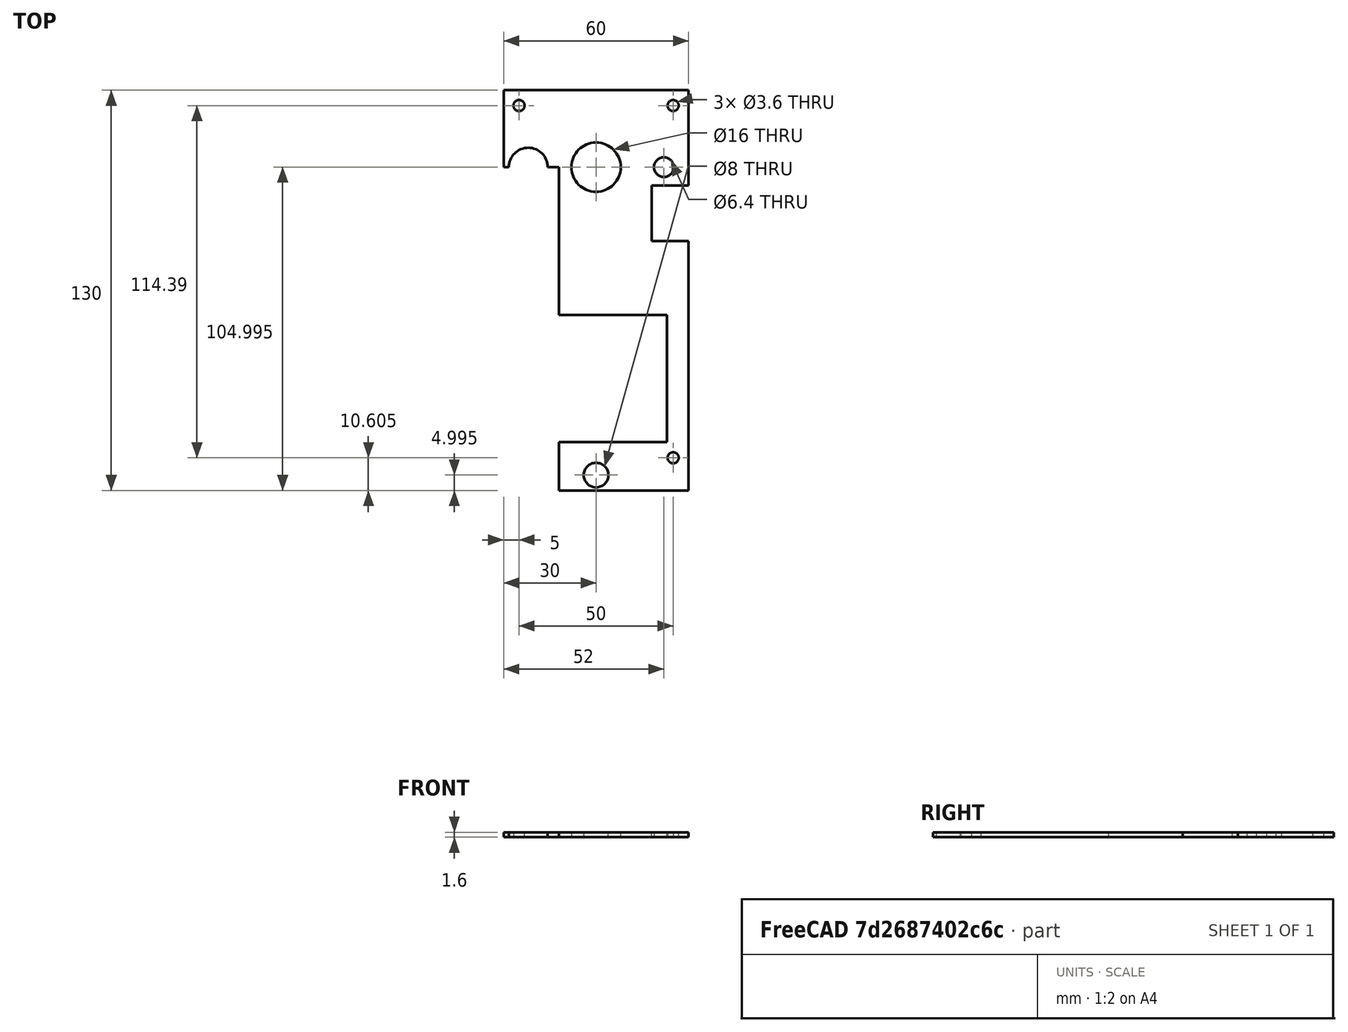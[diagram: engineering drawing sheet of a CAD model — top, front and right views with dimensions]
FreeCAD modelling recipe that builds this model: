
FCSTD DOCUMENT  (FreeCAD 0.18.4R)
Label: acrylic_head_pnp
License: All rights reserved
LicenseURL: http://en.wikipedia.org/wiki/All_rights_reserved
objects: Sketcher::SketchObject×1, PartDesign::Pad×1, PartDesign::Body×1
note: 4 computed .brp shape members not serialized (recipe doc carries the construction recipe); baked Part::Feature solids carry a one-line shape summary decoded from their .brp

FEATURE [Sketcher::SketchObject] Sketch
  MapMode = 5
  Support = -> [XY_Plane]
  sketch-geometry (24):
    g0: Circle CenterX=0 CenterY=39.8952 CenterZ=0 NormalX=0 NormalY=0 NormalZ=1 AngleXU=0 Radius=8
    g1: Circle CenterX=22 CenterY=39.8952 CenterZ=0 NormalX=0 NormalY=0 NormalZ=1 AngleXU=0 Radius=3.2
    g2: ArcOfCircle CenterX=-22 CenterY=39.8952 CenterZ=0 NormalX=0 NormalY=0 NormalZ=1 AngleXU=0 Radius=6.28949 StartAngle=4e-16 EndAngle=3.14159
    g3: LineSegment StartX=-28.2895 StartY=39.8952 StartZ=0 EndX=-30 EndY=39.8952 EndZ=0
    g4: LineSegment StartX=-15.7105 StartY=39.8952 StartZ=0 EndX=-12 EndY=39.8952 EndZ=0
    g5: LineSegment StartX=-30 StartY=39.8952 StartZ=0 EndX=-30 EndY=64.8952 EndZ=0
    g6: LineSegment StartX=-12 StartY=39.8952 StartZ=0 EndX=-12 EndY=-8.10484 EndZ=0
    g7: LineSegment StartX=-12 StartY=-8.10484 StartZ=0 EndX=-3.49057 EndY=-8.10484 EndZ=0
    g8: LineSegment StartX=3.49058 StartY=-8.10484 StartZ=0 EndX=23 EndY=-8.10484 EndZ=0
    g9: LineSegment StartX=23 StartY=-8.10484 StartZ=0 EndX=23 EndY=-49.4148 EndZ=0
    g10: LineSegment StartX=23 StartY=-49.4148 StartZ=0 EndX=-12 EndY=-49.4148 EndZ=0
    g11: LineSegment StartX=-12 StartY=-49.4148 StartZ=0 EndX=-12 EndY=-65.1048 EndZ=0
    g12: LineSegment StartX=30 StartY=-65.1048 StartZ=0 EndX=-12 EndY=-65.1048 EndZ=0
    g13: LineSegment StartX=30 StartY=33.8952 StartZ=0 EndX=18 EndY=33.8952 EndZ=0
    g14: LineSegment StartX=30 StartY=33.8952 StartZ=0 EndX=30 EndY=64.8952 EndZ=0
    g15: LineSegment StartX=18 StartY=33.8952 StartZ=0 EndX=18 EndY=15.8952 EndZ=0
    g16: LineSegment StartX=18 StartY=15.8952 StartZ=0 EndX=30 EndY=15.8952 EndZ=0
    g17: LineSegment StartX=-3.49058 StartY=-8.10484 StartZ=0 EndX=3.49058 EndY=-8.10484 EndZ=0
    g18: Circle CenterX=0 CenterY=-60.1048 CenterZ=0 NormalX=0 NormalY=0 NormalZ=1 AngleXU=0 Radius=4
    g19: Circle CenterX=25 CenterY=-54.4948 CenterZ=0 NormalX=0 NormalY=0 NormalZ=1 AngleXU=0 Radius=1.8
    g20: Circle CenterX=25 CenterY=59.8952 CenterZ=0 NormalX=0 NormalY=0 NormalZ=1 AngleXU=0 Radius=1.8
    g21: LineSegment StartX=30 StartY=15.8952 StartZ=0 EndX=30 EndY=-65.1048 EndZ=0
    g22: LineSegment StartX=-30 StartY=64.8952 StartZ=0 EndX=30 EndY=64.8952 EndZ=0
    g23: Circle CenterX=-25 CenterY=59.8952 CenterZ=0 NormalX=0 NormalY=0 NormalZ=1 AngleXU=0 Radius=1.8
  constraints (63):
    c: PointOnObject(g0,g-2)
    c: Radius(g0) = 8
    c: Radius(g1) = 3.2
    c: Horizontal(g0,g1)
    c: Coincident(g3,g2)
    c: Distance(g1,g2) = 44
    c: Coincident(g4,g2)
    c: Horizontal(g4)
    c: Horizontal(g3,g2)
    c: DistanceX(g3,g4) = 18
    c: Coincident(g5,g3)
    c: Vertical(g5)
    c: Coincident(g6,g4)
    c: Vertical(g6)
    c: DistanceY(g6,g6) = 48
    c: Horizontal(g3,g2)
    c: Horizontal(g0,g4)
    c: Coincident(g7,g6)
    c: Horizontal(g7)
    c: Horizontal(g8)
    c: Coincident(g9,g8)
    c: Vertical(g9)
    c: Coincident(g10,g9)
    c: Horizontal(g10)
    c: DistanceX(g10,g10) = 35
    c: Coincident(g11,g10)
    c: Coincident(g12,g11)
    c: Horizontal(g12)
    c: Horizontal(g13)
    c: Vertical(g14)
    c: Distance(g14) = 31
    c: Distance(g5,g14) = 60
    c: Coincident(g15,g13)
    c: Vertical(g15)
    c: Coincident(g16,g15)
    c: Horizontal(g16)
    c: Distance(g12,g14) = 130
    c: DistanceY(g15,g15) = 18
    c: Horizontal(g8,g7)
    c: Distance(g8,g9) = 41.31
    c: Perpendicular(g12,g11)
    c: Coincident(g17,g7)
    c: Coincident(g17,g8)
    c: PointOnObject(g18,g-2)
    c: Distance(g18,g12) = 5
    c: Radius(g18) = 4
    c: Radius(g19) = 1.8
    c: Distance(g19,g12) = 10.61
    c: Distance(g20,g14) = 5
    c: Radius(g20) = 1.8
    c: Symmetric(g1,g2,g-2)
    c: Symmetric(g14,g5,g-2)
    c: Distance(g13) = 12
    c: Distance(g16) = 12
    c: Coincident(g14,g13)
    c: Coincident(g21,g16)
    c: Coincident(g21,g12)
    c: Vertical(g21)
    c: Coincident(g22,g5)
    c: Coincident(g22,g14)
    c: Radius(g23) = 1.8
    c: Distance(g23,g22) = 5
    c: Distance(g23,g5) = 5
FEATURE [PartDesign::Pad] Pad
  Length = 1.6
  Length2 = 100
  Profile = -> Sketch
  Type = 0
FEATURE [PartDesign::Body] Body
  Group = -> [Sketch,Pad]
  Origin = -> Origin
  Tip = -> Pad
